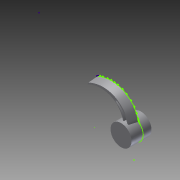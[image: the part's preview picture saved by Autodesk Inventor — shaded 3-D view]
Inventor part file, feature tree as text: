
AUTODESK INVENTOR PART (.ipt)
format: ipt  version: 2013 (Build 170138000, 138)  size: 236,032 bytes
history: native  units: in
note: dims shown in document units (in); Inventor stores cm internally (conversion verified against a paired STEP export)
features: sketch x5, extrude x2, loft x2, plane x1
ambient origin geometry x8: Origin, YZ Plane, XZ Plane, XY Plane, X Axis, Y Axis, Z Axis, Center Point
bodies: Solid1 (feature_tree)
feature tree (10):
  sketch  "Sketch1"  dims[d0=0.551in d1=0.0in d4=0.0in d5=90.0deg]
  extrude  "Extrusion1"  TaperAngle=0.0deg  [1 undecoded]
  loft  "Loft1"
  sketch  "Sketch3"  dims[d9=0.0in d10=90.0deg d11=0.0in d12=90.0deg]
  plane  "Work Plane1"
  loft  "Loft2"
  extrude  "Extrusion3"  [1 undecoded]
  sketch  "Sketch2"  dims[d6=0.0in d7=90.0deg d8=-0.246in]
  sketch  "Sketch4"  dims[d13=0.099in d14=-0.0103in]
  sketch  "Sketch5"
note: 2 required parameter values undecoded (feature->parameter linkage not recoverable at this tier; creation-order binding heuristic only, values carry confidence <= 0.55)
